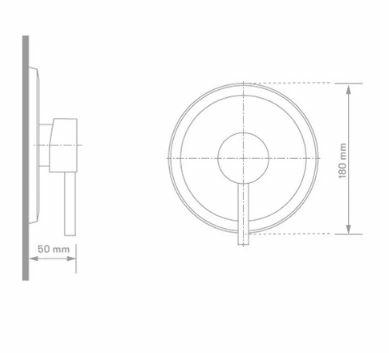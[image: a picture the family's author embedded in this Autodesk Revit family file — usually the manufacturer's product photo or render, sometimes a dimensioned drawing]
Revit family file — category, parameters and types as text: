
# Revit family: 01-2458-11 TOALLERO ARO METALICO QUADRA
name_source: partatom
category: Plumbing Fixtures
revit_build: Autodesk Revit 2018 (Build: 20170223_1515(x64)
units: mm (PartAtom-declared; Revit-internal decimal feet)

## family parameters
Cut with Voids When Loaded = No
Host = Face
OmniClass Number = 23.31.11.00
Part Type = Normal
Room Calculation Point = No
Round Connector Dimension = Use Diameter
Shared = No

## types (1)
- 01-2458-11
    Alto toallero = 116 mm  [stored 0.380577 ft]
    Ancho Soporte = 22 mm  [stored 0.0721785 ft]
    Ancho toallero = 230 mm  [stored 0.754593 ft]
    CW Connection = Yes
    Default Elevation = 0 mm  [stored 0 ft]
    Description = TOALLERO
    HW Connection = Yes
    Link Ficha Tecnica = http://infotecnica.gricol.com
    Manufacturer = Gricol
    Model = 01-2458-11
    Product Name = TOALLERO ARO METALICO QUADRA
    Profundidad = 75 mm  [stored 0.246063 ft]
    Soporte y Toallero = Metal Laton Cromado
    Type Image = TOALLERO ARO METALICO QUADRA.JPG
    URL = https://www.gricol.com
    Vent Connection = No
    Waste Connection = No

note: [stored X ft] marks values corroborated as IEEE doubles in the binary element streams (Revit-internal decimal feet)

## geometry (parser evidence)
native form markers: Blend x2, Sweep x4
no freeform markers — native parametric forms only
